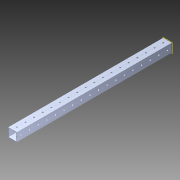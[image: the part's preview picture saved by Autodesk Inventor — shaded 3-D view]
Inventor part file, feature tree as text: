
AUTODESK INVENTOR PART (.ipt)
format: ipt  version: 2014 (Build 180170000, 170)  size: 1,288,704 bytes
history: native  units: in
note: dims shown in document units (in); Inventor stores cm internally (conversion verified against a paired STEP export)
features: extrude x3, sketch x3, pattern_circular x1, other x1, plane x1, imported_body x1
ambient origin geometry x8: Origin, YZ Plane, XZ Plane, XY Plane, X Axis, Y Axis, Z Axis, Center Point
bodies: Body1 (feature_tree)
feature tree (10):
  pattern_circular  "CirPattern2"
  other  "217-3426-STEP1"
  plane  "Work Plane1"
  extrude  "Extrusion1"  Depth=3937.0079in TaperAngle=0.0deg
  extrude  "Extrusion2"  Depth=1.0in TaperAngle=0.0deg
  extrude  "Extrusion3"  [1 undecoded]
  imported_body  "Base1"
  sketch  "Sketch1"  dims[d0=-21.0in d1=3937.0079in d2=0.0in]
  sketch  "Sketch3"  dims[d3=1.0in d4=0.0in d5=2.0in d6=0.0in]
  sketch  "Sketch4"
note: 1 required parameter value undecoded (feature->parameter linkage not recoverable at this tier; creation-order binding heuristic only, values carry confidence <= 0.55)
